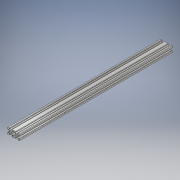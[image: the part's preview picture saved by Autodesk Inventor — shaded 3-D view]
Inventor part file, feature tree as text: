
AUTODESK INVENTOR PART (.ipt)
format: ipt  version: 2019 (Build 230136000, 136)  size: 222,208 bytes
history: native  units: mm
features: extrude x1, sketch x1
ambient origin geometry x8: Origin, YZ Plane, XZ Plane, XY Plane, X Axis, Y Axis, Z Axis, Center Point
bodies: Body1 (feature_tree)
feature tree (2):
  extrude  "Extrusion5"  [1 undecoded]
  sketch  "Sketch1"  dims[d8=500.0mm d9=0.0mm]
note: 1 required parameter value undecoded (feature->parameter linkage not recoverable at this tier; creation-order binding heuristic only, values carry confidence <= 0.55)
